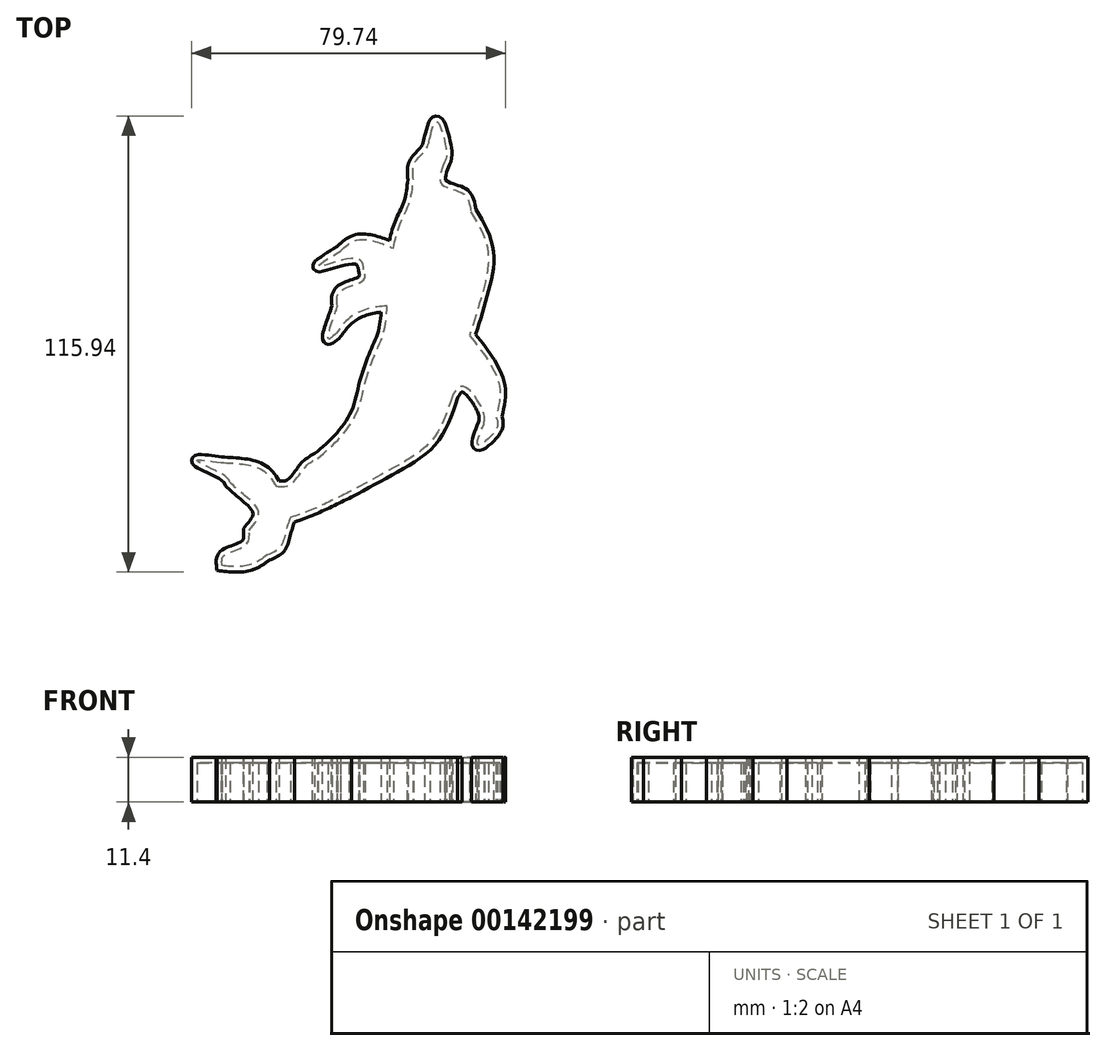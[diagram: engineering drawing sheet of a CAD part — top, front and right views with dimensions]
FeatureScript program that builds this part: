
annotation { "Feature Type Name" : "Feature", "Feature Type Description" : "" }
export const myFeature = defineFeature(function(context is Context, id is Id, definition is map)
    precondition{}
    {
        {
            var Q0;
            Q0=qCreatedBy(makeId("Top.planeOp"),FACE);
            var sketch = newSketch(context, id + "F0", { "sketchPlane" : qUnion([Q0])});
            skFitSpline(sketch, "E0", {"points": [v(-159.78, -261.58) * mm, v(-157.2, -249.22) * mm, v(-131.16, -236.58) * mm, v(-126.96, -218.72) * mm]});
            skFitSpline(sketch, "E1", {"points": [v(-126.96, -218.72) * mm, v(-115.61, -196.64) * mm, v(-134.32, -175.09) * mm, v(-150.02, -161.2) * mm]});
            skFitSpline(sketch, "E2", {"points": [v(-150.02, -161.2) * mm, v(-156.58, -152.81) * mm, v(-189.82, -134.82) * mm, v(-160.78, -136.88) * mm]});
            skFitSpline(sketch, "E3", {"points": [v(-160.78, -136.88) * mm, v(-136.23, -138.5) * mm, v(-110.8, -146.01) * mm, v(-94.45, -165.45) * mm]});
            skFitSpline(sketch, "E4", {"points": [v(-94.45, -165.45) * mm, v(-77.24, -163.56) * mm, v(-59.52, -142.59) * mm, v(-44.35, -131.69) * mm]});
            skFitSpline(sketch, "E5", {"points": [v(-44.35, -131.69) * mm, v(-17.33, -107.2) * mm, v(3.35, -75.9) * mm, v(12.95, -40.55) * mm]});
            skFitSpline(sketch, "E6", {"points": [v(12.95, -40.55) * mm, v(23.53, -10.05) * mm, v(35.64, 20.28) * mm, v(39.87, 52.48) * mm]});
            skFitSpline(sketch, "E7", {"points": [v(39.87, 52.48) * mm, v(17.47, 49.3) * mm, v(-6.22, 37.38) * mm, v(-21.28, 19.85) * mm]});
            skFitSpline(sketch, "E8", {"points": [v(-21.28, 19.85) * mm, v(-31.27, 13.25) * mm, v(-22.5, 44.83) * mm, v(-20.13, 52.43) * mm]});
            skFitSpline(sketch, "E9", {"points": [v(-20.13, 52.43) * mm, v(-16.45, 70.73) * mm, v(11.16, 83.93) * mm, v(11.68, 96.54) * mm]});
            skFitSpline(sketch, "E10", {"points": [v(11.68, 96.54) * mm, v(3.2, 109.9) * mm, v(-42.91, 100.4) * mm, v(-16.7, 118.99) * mm]});
            skFitSpline(sketch, "E11", {"points": [v(-16.7, 118.99) * mm, v(2.14, 132.07) * mm, v(27.3, 130.2) * mm, v(47.5, 122.38) * mm]});
            skFitSpline(sketch, "E12", {"points": [v(47.5, 122.38) * mm, v(55.05, 150.23) * mm, v(66.63, 176.88) * mm, v(71.73, 205.38) * mm]});
            skFitSpline(sketch, "E13", {"points": [v(71.73, 205.38) * mm, v(73.13, 225.32) * mm, v(86.58, 241.57) * mm, v(91.8, 256.56) * mm]});
            skFitSpline(sketch, "E14", {"points": [v(91.8, 256.56) * mm, v(100.25, 275.78) * mm, v(111.74, 236.68) * mm, v(109.24, 226.65) * mm]});
            skFitSpline(sketch, "E15", {"points": [v(109.24, 226.65) * mm, v(105.7, 200.35) * mm, v(132.22, 188.32) * mm, v(141.01, 166.77) * mm]});
            skFitSpline(sketch, "E16", {"points": [v(141.01, 166.77) * mm, v(161.84, 119.3) * mm, v(154.27, 64.9) * mm, v(139.7, 16.79) * mm]});
            skFitSpline(sketch, "E17", {"points": [v(139.7, 16.79) * mm, v(160.7, -11.17) * mm, v(175.98, -45.99) * mm, v(171.8, -81.65) * mm]});
            skFitSpline(sketch, "E18", {"points": [v(171.8, -81.65) * mm, v(172.03, -96.04) * mm, v(150.19, -115.62) * mm, v(156.95, -89.97) * mm]});
            skFitSpline(sketch, "E19", {"points": [v(156.95, -89.97) * mm, v(156, -74.34) * mm, v(131.41, -44.68) * mm, v(118.81, -56.32) * mm]});
            skFitSpline(sketch, "E20", {"points": [v(118.81, -56.32) * mm, v(94.16, -109.7) * mm, v(44.07, -145.32) * mm, v(-6.17, -172.73) * mm]});
            skFitSpline(sketch, "E21", {"points": [v(-6.17, -172.73) * mm, v(-29.4, -183.94) * mm, v(-52.95, -194.75) * mm, v(-77.18, -203.44) * mm]});
            skFitSpline(sketch, "E22", {"points": [v(-77.18, -203.44) * mm, v(-82.74, -219.99) * mm, v(-89.25, -239.13) * mm, v(-105.5, -248.9) * mm]});
            skFitSpline(sketch, "E23", {"points": [v(-105.5, -248.9) * mm, v(-121.47, -258.97) * mm, v(-141.1, -262.79) * mm, v(-159.78, -261.58) * mm]});
            skSolve(sketch);
        }
        {
            var Q0;
            Q0 = qSketchRegion(id + "F0", true);
            extrude(context, id + "F1", {"entities" : qUnion([Q0]), "depth" : 42.68 * mm});
        }
        {
            var Q0;
            Q0=makeQuery(id+"F1.opExtrude","SWEPT_BODY",BODY,{"disambiguationData":[OSD([sQuery(id+"F0.wireOp",EDGE,"E0"),sQuery(id+"F0.wireOp",EDGE,"E1"),sQuery(id+"F0.wireOp",EDGE,"E2"),sQuery(id+"F0.wireOp",EDGE,"E3"),sQuery(id+"F0.wireOp",EDGE,"E4"),sQuery(id+"F0.wireOp",EDGE,"E5"),sQuery(id+"F0.wireOp",EDGE,"E6"),sQuery(id+"F0.wireOp",EDGE,"E7"),sQuery(id+"F0.wireOp",EDGE,"E8"),sQuery(id+"F0.wireOp",EDGE,"E9"),sQuery(id+"F0.wireOp",EDGE,"E10"),sQuery(id+"F0.wireOp",EDGE,"E11"),sQuery(id+"F0.wireOp",EDGE,"E12"),sQuery(id+"F0.wireOp",EDGE,"E13"),sQuery(id+"F0.wireOp",EDGE,"E14"),sQuery(id+"F0.wireOp",EDGE,"E15"),sQuery(id+"F0.wireOp",EDGE,"E16"),sQuery(id+"F0.wireOp",EDGE,"E17"),sQuery(id+"F0.wireOp",EDGE,"E18"),sQuery(id+"F0.wireOp",EDGE,"E19"),sQuery(id+"F0.wireOp",EDGE,"E20"),sQuery(id+"F0.wireOp",EDGE,"E21"),sQuery(id+"F0.wireOp",EDGE,"E22"),sQuery(id+"F0.wireOp",EDGE,"E23")])]});
            var Q1;
            Q1=qCreatedBy(makeId("Origin.pointOp"),VERTEX);
            transform(context, id + "F2", {"entities" : qUnion([Q0]), "transformType" : TransformType.SCALE_UNIFORMLY, "scale" : 0.2, "scalePoint" : qUnion([Q1]), "makeCopy" : false});
        }
        {
            var Q0;
            Q0=qCreatedBy(makeId("Top.planeOp"),FACE);
            cPlane(context, id + "F3", {"entities" : qUnion([Q0]), "cplaneType" : CPlaneType.OFFSET, "offset" : 10 * mm, "width" : 150 * mm, "height" : 150 * mm});
        }
        {
            var Q0;
            Q0=makeQuery(id+"F1.opExtrude","CAP_FACE",FACE,{"disambiguationData":[OSD([sQuery(id+"F0.wireOp",EDGE,"E0"),sQuery(id+"F0.wireOp",EDGE,"E1"),sQuery(id+"F0.wireOp",EDGE,"E2"),sQuery(id+"F0.wireOp",EDGE,"E3"),sQuery(id+"F0.wireOp",EDGE,"E4"),sQuery(id+"F0.wireOp",EDGE,"E5"),sQuery(id+"F0.wireOp",EDGE,"E6"),sQuery(id+"F0.wireOp",EDGE,"E7"),sQuery(id+"F0.wireOp",EDGE,"E8"),sQuery(id+"F0.wireOp",EDGE,"E9"),sQuery(id+"F0.wireOp",EDGE,"E10"),sQuery(id+"F0.wireOp",EDGE,"E11"),sQuery(id+"F0.wireOp",EDGE,"E12"),sQuery(id+"F0.wireOp",EDGE,"E13"),sQuery(id+"F0.wireOp",EDGE,"E14"),sQuery(id+"F0.wireOp",EDGE,"E15"),sQuery(id+"F0.wireOp",EDGE,"E16"),sQuery(id+"F0.wireOp",EDGE,"E17"),sQuery(id+"F0.wireOp",EDGE,"E18"),sQuery(id+"F0.wireOp",EDGE,"E19"),sQuery(id+"F0.wireOp",EDGE,"E20"),sQuery(id+"F0.wireOp",EDGE,"E21"),sQuery(id+"F0.wireOp",EDGE,"E22"),sQuery(id+"F0.wireOp",EDGE,"E23")])],"isStart":false});
            var Q1;
            Q1=qCreatedBy(id+"F3.planeOp",FACE);
            extrude(context, id + "F4", {"entities" : qUnion([Q0]), "operationType" : NewBodyOperationType.ADD, "endBound" : BoundingType.UP_TO_SURFACE, "endBoundEntityFace" : qUnion([Q1]), "depth" : 25 * mm});
        }
        {
            var Q0;
            Q0=makeQuery(id+"F4.opExtrude","CAP_FACE",FACE,{"disambiguationData":[OSD([dummyQuery(id+"F3.planeOp",FACE)])],"isStart":false});
            var Q1;
            Q1=makeQuery(id+"F1.opExtrude","CAP_FACE",FACE,{"disambiguationData":[OSD([sQuery(id+"F0.wireOp",EDGE,"E0"),sQuery(id+"F0.wireOp",EDGE,"E1"),sQuery(id+"F0.wireOp",EDGE,"E2"),sQuery(id+"F0.wireOp",EDGE,"E3"),sQuery(id+"F0.wireOp",EDGE,"E4"),sQuery(id+"F0.wireOp",EDGE,"E5"),sQuery(id+"F0.wireOp",EDGE,"E6"),sQuery(id+"F0.wireOp",EDGE,"E7"),sQuery(id+"F0.wireOp",EDGE,"E8"),sQuery(id+"F0.wireOp",EDGE,"E9"),sQuery(id+"F0.wireOp",EDGE,"E10"),sQuery(id+"F0.wireOp",EDGE,"E11"),sQuery(id+"F0.wireOp",EDGE,"E12"),sQuery(id+"F0.wireOp",EDGE,"E13"),sQuery(id+"F0.wireOp",EDGE,"E14"),sQuery(id+"F0.wireOp",EDGE,"E15"),sQuery(id+"F0.wireOp",EDGE,"E16"),sQuery(id+"F0.wireOp",EDGE,"E17"),sQuery(id+"F0.wireOp",EDGE,"E18"),sQuery(id+"F0.wireOp",EDGE,"E19"),sQuery(id+"F0.wireOp",EDGE,"E20"),sQuery(id+"F0.wireOp",EDGE,"E21"),sQuery(id+"F0.wireOp",EDGE,"E22"),sQuery(id+"F0.wireOp",EDGE,"E23")])],"isStart":true});
            shell(context, id + "F5", {"entities" : qUnion([Q0, Q1]), "thickness" : 1.4 * mm, "oppositeDirection" : true});
        }
    });
